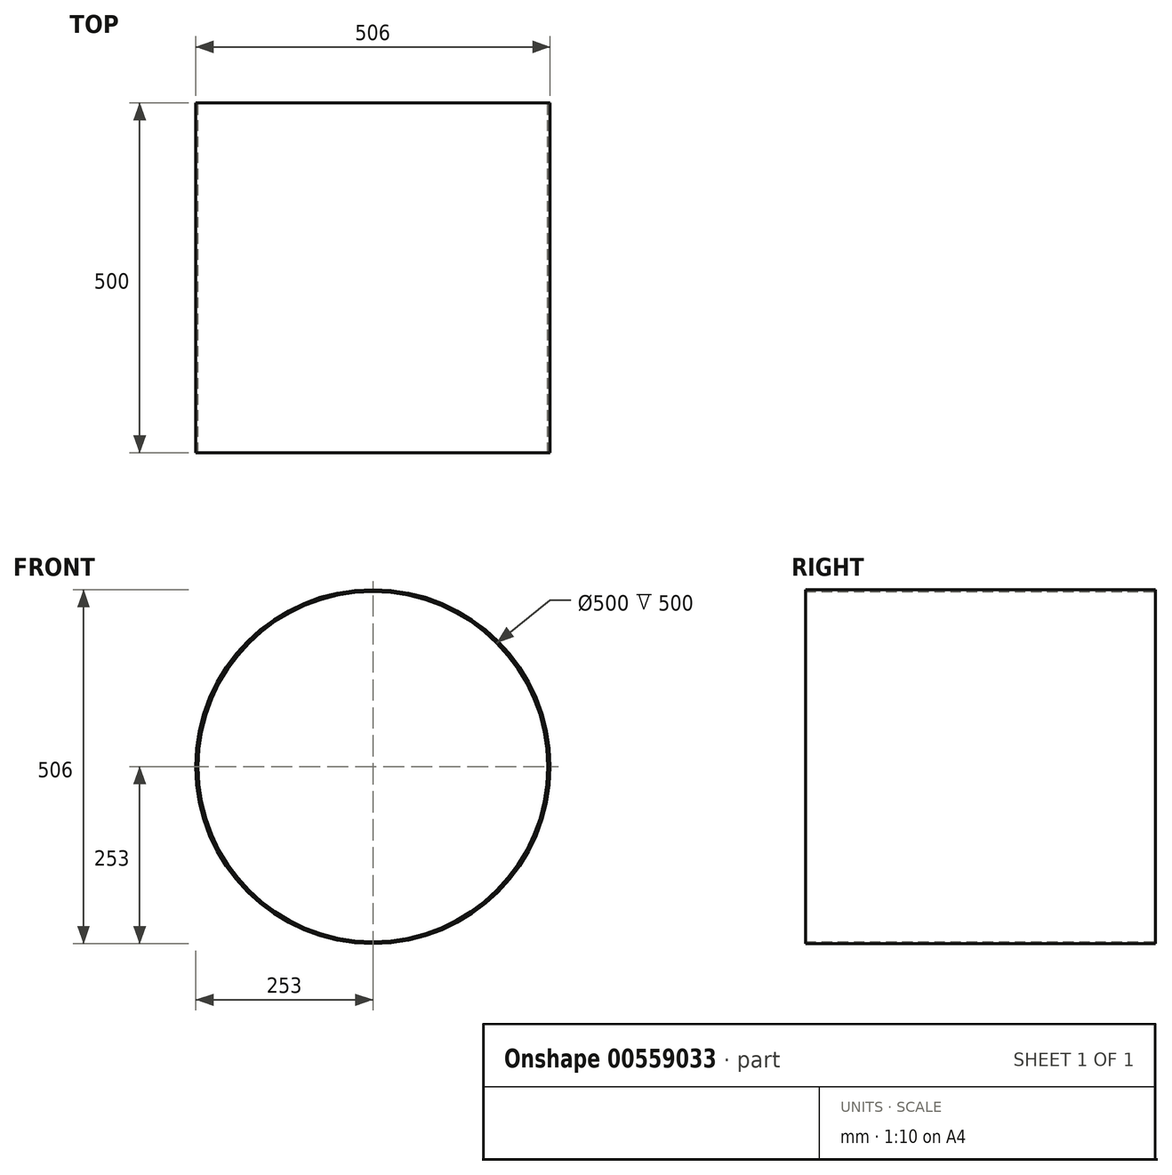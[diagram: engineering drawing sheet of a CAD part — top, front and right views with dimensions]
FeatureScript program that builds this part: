
annotation { "Feature Type Name" : "Feature", "Feature Type Description" : "" }
export const myFeature = defineFeature(function(context is Context, id is Id, definition is map)
    precondition{}
    {
        {
            var Q0;
            Q0=qCreatedBy(makeId("Front.planeOp"),FACE);
            var sketch = newSketch(context, id + "F0", { "sketchPlane" : qUnion([Q0])});
            skCircle(sketch, "E0", {"center": v(0, 0) * mm, "radius": 250 * mm});
            skCircle(sketch, "E1", {"center": v(0, 0) * mm, "radius": 253 * mm});
            skSolve(sketch);
        }
        {
            var Q0;
            Q0=makeQuery(id+"F0.imprint","IMPRINT",FACE,{"disambiguationData":[TD([[makeQuery(id+"F0.imprint","IMPRINT",EDGE,{"derivedFrom":sQuery(id+"F0.wireOp",EDGE,"E0")}),-1.0]])]});
            extrude(context, id + "F1", {"entities" : qUnion([Q0]), "depth" : 500 * mm, "offsetDistance" : 25 * mm});
        }
    });
